# Revit family: RN 15090 Systemtrenner CA
name_source: partatom
category: Rohrzubehör
units: mm (PartAtom-declared; Revit-internal decimal feet)

## family parameters
Arbeitsebenenbasiert = Nein
Beim Laden mit Abzugskörper schneiden = Nein
Bemaßung runder Anschluss = Durchmesser verwenden
Gemeinsam genutzt = Nein
Immer vertikal = Ja
Teiletyp = Ventil - Zerlegung in

## types (2) — shared parameters
1.010.00.2 Blattnummer der Richtlinie = 17
1.010.00.3 Ausgabedatum (Monat) der Richtlinie = 201601
1.010.00.4 Herstellername = R. Nussbaum AG
1.010.00.5 Revisionsdatum der Datei = 20190528
1.010.00.6 Webadresse des Herstellers = http://www.nussbaum.ch
1.100.00.3 Sortiernummer für Anzeigereihenfolge = 4
1.100.00.4 Produktbezeichnung = Sicherungs- und Ringleitungsarmaturen
1.960/3L.00.8 Link (URL) = https://www.nussbaum.ch
17.700.00.4 Armaturentyp = 7
17.700.00.6 kvs-Wert [m3/h] = 22
17.700.00.7 Maximale Betriebstemperatur TB [°C] = 60
17.700.00.8 Maximaler Betriebsdruck (Arbeitsdruck) ps [1.0 · 105 Pa] = 10
Connector Visibility = Nein
EnclosingSpace Visibility = Nein
Hersteller = R. Nussbauzm AG
URL = https://www.nussbaum.ch

## per-type parameters (varying)
| type | 1.800.00.3 TGA-Nummer | 1.810.00.3 Hersteller-Bestellnummer | 1.810.00.4 DATANORM-Nummer | 1.810.00.6 GTIN-Nummer | 17.700.00.30 Produktbeschreibung | 17.700.00.5 Nennweite DN | CONNECTOR0_DIAMETER_dX_0r | CONNECTOR0_dX_00 | CONNECTOR0_dX_01 | CONNECTOR0_ref_dX | CONNECTOR1_DIAMETER_dX_0r | CONNECTOR1_dX_00 | CONNECTOR1_dX_01 | CONNECTOR1_ref_dX | Modell | R. Nussbaum AG 15090.04 de Visibility | R. Nussbaum AG 15090.05 de Visibility | Typenkommentare |
| DN 15 | 0040300000000000000000000000010070000000000000000100000000 | 15090.04 | 15090.04 | 7612945743640 | 15090.04, Systemtrenner CA, mit Anschlussverschraubungen, DN=15, R=½ | 15 | 15 mm  [stored 0.0492126 ft] | 68 mm | 55 mm  [stored 0.180446 ft] | 68 mm | 15 mm  [stored 0.0492126 ft] | 55 mm  [stored 0.180446 ft] | 68 mm | 68 mm | 15090.04 | Ja | Nein | Systemtrenner CADN 15 |
| DN 20 | 0040300000000000000000000000010070000000000000000200000000 | 15090.05 | 15090.05 | 7612945743657 | 15090.05, Systemtrenner CA, mit Anschlussverschraubungen, DN=20, R=¾ | 20 | 20 mm | 71 mm | 56 mm | 71 mm | 20 mm | 56 mm | 71 mm | 71 mm | 15090.05 | Nein | Ja | Systemtrenner CADN 20 |

note: [stored X ft] marks values corroborated as IEEE doubles in the binary element streams (Revit-internal decimal feet)

## geometry (parser evidence)
native form markers: Sweep x1
no freeform markers — native parametric forms only
